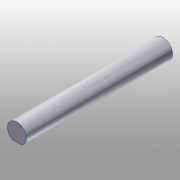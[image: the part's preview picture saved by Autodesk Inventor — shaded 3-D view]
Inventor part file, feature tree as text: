
AUTODESK INVENTOR PART (.ipt)
format: ipt  version: 2015 (Build 190159000, 159)  size: 83,456 bytes
history: native  units: mm
features: other x3, sketch x2
ambient origin geometry x8: Origin, YZ Plane, XZ Plane, XY Plane, X Axis, Y Axis, Z Axis, Center Point
bodies: Solid1 (feature_tree)
feature tree (5):
  other  "307-320.ipt"
  other  "Solid1::307-320.ipt"
  other  "TaggingFeature1"
  sketch  "Sketch1"  dims[d0=10.0mm]
  sketch  "Sketch2"
